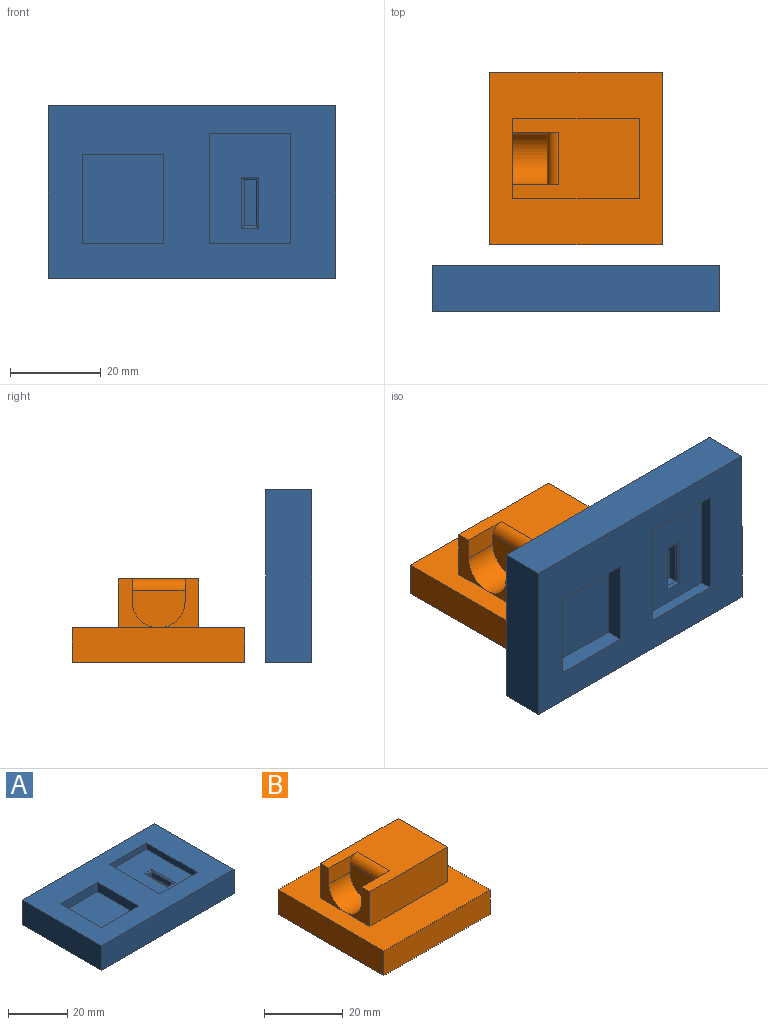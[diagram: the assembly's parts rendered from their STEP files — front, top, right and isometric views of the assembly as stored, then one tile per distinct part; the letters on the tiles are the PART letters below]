
ASSEMBLY  parts=2 mates=1
PART A: 25 faces, bbox 63.5x38.1x10.2 mm
  f0: plane 24.33x17.91mm, normal (0,0,1), area 394.4mm2, adj f12,f13,f14,f15,f21,f22,f23,f24
  f1: plane 63.5x38.1mm, normal (0,0,1), area 1631.1mm2, adj f2,f3,f4,f5,f7,f8,f9,f10
  f2: plane 63.5x10.16mm, normal (0,1,0), area 645.2mm2, adj f1,f3,f5,f6
  f3: plane 38.1x10.16mm, normal (-1,0,0), area 387.1mm2, adj f1,f2,f4,f6
  f4: plane 63.5x10.16mm, normal (0,-1,0), area 645.2mm2, adj f1,f3,f5,f6
  f5: plane 38.1x10.16mm, normal (1,0,0), area 387.1mm2, adj f1,f2,f4,f6
  f6: plane 63.5x38.1mm, normal (0,0,-1), area 2419.3mm2, adj f2,f3,f4,f5
  f7: plane 17.91x3.81mm, normal (0,-1,0), area 68.2mm2, adj f1,f8,f10,f11
  f8: plane 19.69x3.81mm, normal (1,0,0), area 75mm2, adj f1,f7,f9,f11
  f9: plane 17.91x3.81mm, normal (0,1,0), area 68.2mm2, adj f1,f8,f10,f11
  f10: plane 19.69x3.81mm, normal (-1,0,0), area 75mm2, adj f1,f7,f9,f11
  f11: plane 19.69x17.91mm, normal (0,0,1), area 352.5mm2, adj f7,f8,f9,f10
  f12: plane 17.91x2.54mm, normal (0,-1,0), area 45.5mm2, adj f0,f1,f13,f15
  f13: plane 24.33x2.54mm, normal (1,0,0), area 61.8mm2, adj f0,f1,f12,f14
  f14: plane 17.91x2.54mm, normal (0,1,0), area 45.5mm2, adj f0,f1,f13,f15
  f15: plane 24.33x2.54mm, normal (-1,0,0), area 61.8mm2, adj f0,f1,f12,f14
  f16: plane 10.16x2.03mm, normal (1,0,0), area 20.6mm2, adj f17,f19,f20,f24
  f17: plane 2.68x2.03mm, normal (0,1,0), area 5.4mm2, adj f16,f18,f20,f22
  f18: plane 10.16x2.03mm, normal (-1,0,0), area 20.6mm2, adj f17,f19,f20,f21
  f19: plane 2.68x2.03mm, normal (0,-1,0), area 5.4mm2, adj f16,f18,f20,f23
  f20: plane 10.16x2.68mm, normal (0,0,1), area 27.2mm2, adj f16,f17,f18,f19
  f21: cylinder r=0.51mm len=11.18mm, axis (0,-1,0), area 8.4mm2, adj f0,f18,f22,f23
  f22: cylinder r=0.51mm len=3.7mm, axis (-1,0,0), area 2.4mm2, adj f0,f17,f21,f24
  f23: cylinder r=0.51mm len=3.7mm, axis (1,0,0), area 2.4mm2, adj f0,f19,f21,f24
  f24: cylinder r=0.51mm len=11.18mm, axis (0,1,0), area 8.4mm2, adj f0,f16,f22,f23
PART B: 17 faces, bbox 38.1x38.1x18.4 mm
  f0: plane 10.78x8.89mm, normal (-1,0,0), area 40.2mm2, adj f1,f4,f11,f13,f14
  f1: plane 27.94x17.78mm, normal (0,0,1), area 378.1mm2, adj f0,f2,f3,f4,f5,f12,f14,f16
  f2: plane 27.94x10.78mm, normal (0,1,0), area 301.2mm2, adj f1,f3,f5,f11
  f3: plane 10.78x8.89mm, normal (-1,0,0), area 40.2mm2, adj f1,f2,f11,f12,f13
  f4: plane 27.94x10.78mm, normal (0,-1,0), area 301.2mm2, adj f0,f1,f5,f11
  f5: plane 17.78x10.78mm, normal (1,0,0), area 191.7mm2, adj f1,f2,f4,f11
  f6: plane 38.1x7.62mm, normal (-1,0,0), area 290.3mm2, adj f7,f9,f10,f11
  f7: plane 38.1x7.62mm, normal (0,-1,0), area 290.3mm2, adj f6,f8,f10,f11
  f8: plane 38.1x7.62mm, normal (1,0,0), area 290.3mm2, adj f7,f9,f10,f11
  f9: plane 38.1x7.62mm, normal (0,1,0), area 290.3mm2, adj f6,f8,f10,f11
  f10: plane 38.1x38.1mm, normal (0,0,-1), area 1451.6mm2, adj f6,f7,f8,f9
  f11: plane 38.1x38.1mm, normal (0,0,1), area 954.8mm2, adj f0,f2,f3,f4,f5,f6,f7,f8
  f12: plane 10.16x4.94mm, normal (0,-1,0), area 39mm2, adj f1,f3,f13,f15,f16
  f13: cylinder r=5.84mm len=11.68mm, axis (-1,0,0), area 139.9mm2, adj f0,f3,f12,f14,f15
  f14: plane 10.16x4.94mm, normal (0,1,0), area 39mm2, adj f0,f1,f13,f15,f16
  f15: plane 11.68x8.24mm, normal (-1,0,0), area 81.6mm2, adj f12,f13,f14,f16
  f16: cylinder r=2.54mm len=11.68mm, axis (0,-1,0), area 46.6mm2, adj f1,f12,f14,f15
PLACE A rot(axis=(1,0,0),90deg) t=(-0.05,-14.19,6.61)mm
PLACE B t=(5.03,0.54,6.61)mm
MATE parallel B.f10 <-> A.f4  axis (0,0,-1) through (24.08,19.59,-1.01)mm
